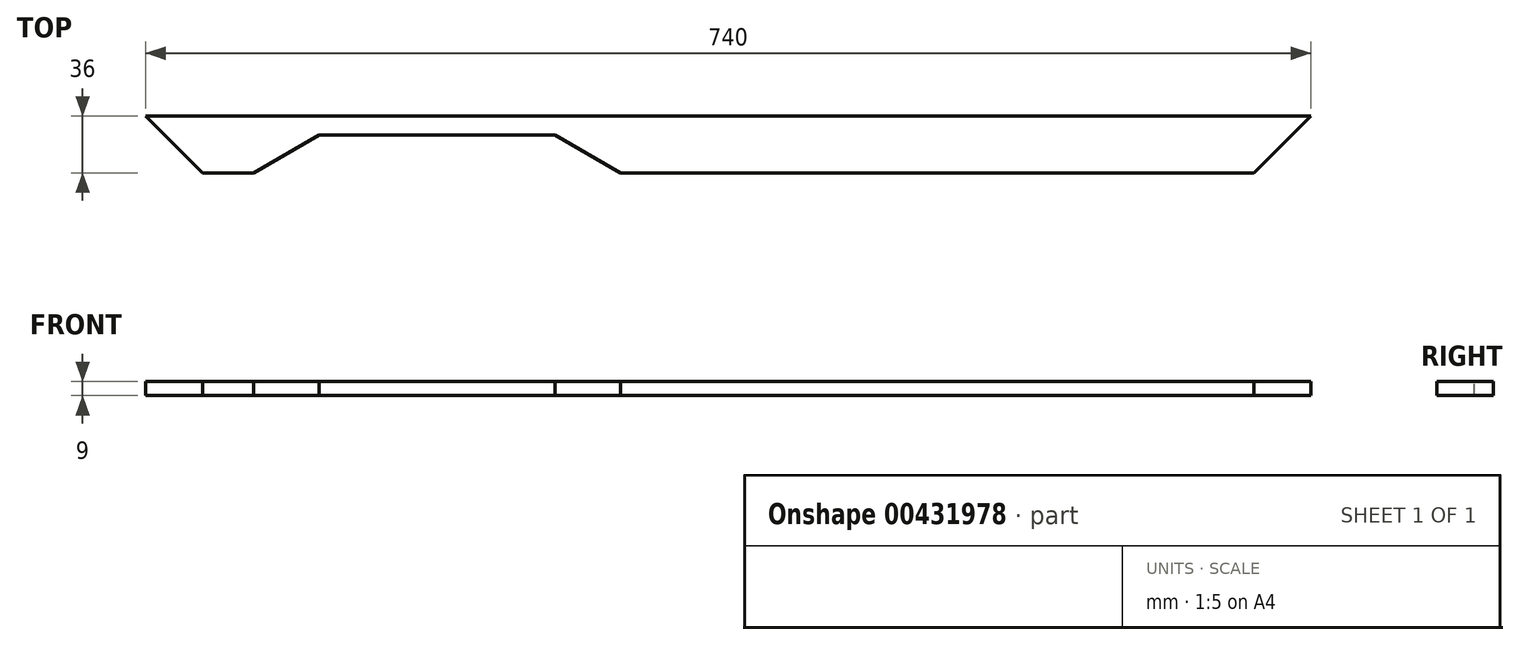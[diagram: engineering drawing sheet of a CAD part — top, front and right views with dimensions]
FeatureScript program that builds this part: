
annotation { "Feature Type Name" : "Feature", "Feature Type Description" : "" }
export const myFeature = defineFeature(function(context is Context, id is Id, definition is map)
    precondition{}
    {
        {
            var Q0;
            Q0=qCreatedBy(makeId("Top.planeOp"),FACE);
            var sketch = newSketch(context, id + "F0", { "sketchPlane" : qUnion([Q0])});
            skLineSegment(sketch, "E0.bottom", {"start": v(-370, 18) * mm, "end": v(370, 18) * mm});
            skLineSegment(sketch, "E0.top", {"start": v(-370, -18) * mm, "end": v(370, -18) * mm});
            skLineSegment(sketch, "E0.left", {"start": v(-370, 18) * mm, "end": v(-370, -18) * mm});
            skLineSegment(sketch, "E0.right", {"start": v(370, 18) * mm, "end": v(370, -18) * mm});
            skPoint(sketch, "E0.middle", {"position": v(0, 0) * mm});
            skSolve(sketch);
        }
        {
            var Q0;
            Q0=makeQuery(id+"F0.imprint","IMPRINT",FACE,{"disambiguationData":[TD([[makeQuery(id+"F0.imprint","IMPRINT",EDGE,{"derivedFrom":sQuery(id+"F0.wireOp",EDGE,"E0.bottom")}),-1.0]])]});
            extrude(context, id + "F1", {"entities" : qUnion([Q0]), "depth" : 9 * mm, "offsetDistance" : 25 * mm});
        }
        {
            var Q0;
            Q0=makeQuery(id+"F1.opExtrude","SWEPT_EDGE",EDGE,{"disambiguationData":[OSD([sQuery(id+"F0.wireOp",EDGE,"E0.top"),sQuery(id+"F0.wireOp",EDGE,"E0.left")])]});
            var Q1;
            Q1=makeQuery(id+"F1.opExtrude","SWEPT_EDGE",EDGE,{"disambiguationData":[OSD([sQuery(id+"F0.wireOp",EDGE,"E0.top"),sQuery(id+"F0.wireOp",EDGE,"E0.right")])]});
            chamfer(context, id + "F2", {"entities" : qUnion([Q0, Q1]), "width" : 36 * mm, "tangentPropagation" : true});
        }
        {
            var Q0;
            Q0=makeQuery(id+"F1.opExtrude","CAP_FACE",FACE,{"disambiguationData":[OSD([sQuery(id+"F0.wireOp",EDGE,"E0.bottom"),sQuery(id+"F0.wireOp",EDGE,"E0.top"),sQuery(id+"F0.wireOp",EDGE,"E0.left"),sQuery(id+"F0.wireOp",EDGE,"E0.right")])],"isStart":false});
            var sketch = newSketch(context, id + "F3", { "sketchPlane" : qUnion([Q0])});
            skLineSegment(sketch, "E1.bottom", {"start": v(-68.43, -18) * mm, "end": v(-301.57, -18) * mm});
            skLineSegment(sketch, "E1.top", {"start": v(-110, 6) * mm, "end": v(-260, 6) * mm});
            skLineSegment(sketch, "E2", {"start": v(-260, 6) * mm, "end": v(-301.57, -18) * mm});
            skLineSegment(sketch, "E3", {"start": v(-110, 6) * mm, "end": v(-68.43, -18) * mm});
            skSolve(sketch);
        }
        {
            var Q0;
            Q0 = qSketchRegion(id + "F3", true);
            extrude(context, id + "F4", {"entities" : qUnion([Q0]), "operationType" : NewBodyOperationType.REMOVE, "endBound" : BoundingType.UP_TO_NEXT, "oppositeDirection" : true, "depth" : 25 * mm, "offsetDistance" : 25 * mm});
        }
    });
